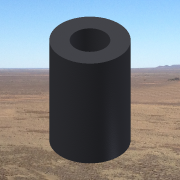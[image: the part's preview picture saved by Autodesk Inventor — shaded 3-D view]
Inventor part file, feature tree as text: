
AUTODESK INVENTOR PART (.ipt)
format: ipt  version: 2014 SP1 (Build 180222100, 222)  size: 123,904 bytes
history: native  units: in
note: dims shown in document units (in); Inventor stores cm internally (conversion verified against a paired STEP export)
features: extrude x1, sketch x1
ambient origin geometry x8: Origin, YZ Plane, XZ Plane, XY Plane, X Axis, Y Axis, Z Axis, Center Point
bodies: Solid1 (feature_tree)
feature tree (2):
  extrude  "Extrusion1"  Depth=2.0in
  sketch  "Sketch1"  dims[d0=8.0in d1=2.0in d2=12.0in d3=0.0in]
